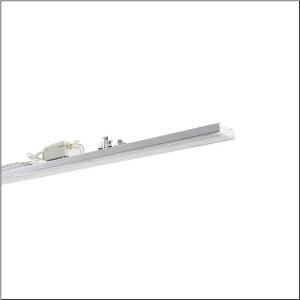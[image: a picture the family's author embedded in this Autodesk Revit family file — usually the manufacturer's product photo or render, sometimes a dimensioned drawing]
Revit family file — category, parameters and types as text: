
# Revit family: licross_11_recessed_mo_51tl14dn325g
name_source: partatom
category: Lighting Fixtures
units: mm (PartAtom-declared; Revit-internal decimal feet)

## family parameters
Cut with Voids When Loaded = No
Host = Face
Light Source = No
Part Type = Normal
Room Calculation Point = No
Round Connector Dimension = Use Diameter
Shared = No

## types (1)
- --- (1 x LED, 2900 lm, 17.6 W, 3000K)
    Apparent Load = 18 VA
    CIE Flux Codes = 56 84 97 100 100
    Color Rendering = 80
    Color Temperature = 3000K
    Default Elevation = 1800 mm
    Description = Licross 11 Recessed MO, luminaire insert, of sheet steel, coil coated, white, length: 1.500mm, width: 66mm, height: 67mm, LED rated luminous flux: 2.900lm, light colour: 830, SDCM (Standard Deviation of Colour Matching)MacAdam ≤ 2 SDCM (initial), control gear: DALI 2, with plug, 5-pole, with phase selection, mains connection: 220..240V, AC, 50/60Hz, rated input power: 17.6W, internal wiring halogen-free, primary light control with lens, of plastic, primary optical cover: cover, of PMMA, light emission: direct distribution, primary light characteristic: asymmetric, protection rating (complete): IP40, insulation class (complete): insulation class I (protective earthing), certification: CE, ENEC, VDE, UKCA, protection symbol: D if used in an environment without relevant dust loads with corresponding accessories, impact resistance: IK06, permissible ambient temperature for indoor applications: -25..+50°C, corresponds to IFS (International Featured Standards) requirements for safety and quality in the food industry, reducing of maximum allowable ambient temperature of 5°C with ceiling mounting, LABS conformity tested according to VDMA 24364:2018-05, The light source and the operating device comply with the requirements of the Ecodesign Regulation (EU) 2019/2020 and are replaceable in accordance with this regulation, packaging unit: 1 piece
    Height = 58 mm
    Lamp = 1 x LED
    Lamp Light Flux = 2900 lm
    Lamp Power = 17.6 W
    Lamp count = 1
    Length = 1500 mm
    Luminous efficacy = 165 lm/W
    Manufacturer = Siteco
    ModVariant = No
    Model = 51TL14DN325G
    Mounting Place = Ceiling
    Mounting Type = Pendant
    Number of Poles = 1
    OnlyDefault = Yes
    Power Factor = 1
    Product Name = Licross 11 Recessed MO
    Product group = luminaire insert | ceiling pendant
    ProductGroupID = 901
    Protection Class = Protection class I
    Protection Degree = IP 40
    RLX_Detail_Level = 1
    RLX_Emergency_Light_Flux = 0 lm
    RLX_Emergency_Type = 0
    RLX_Emergency_Type_DB = No
    RlxData = <blob elided: 24953 chars, md5=e817cd5a>
    Socket = socket
    Standby Power = 0 W
    System Light Flux = 2900 lm
    System Power = 18 W
    Type Comments = factory setting: luminous flux: 100 % | dim-lin: 254 | 114 mA
    Type Image = l_1296930.jpg
    URL = http://relux.com
    VarID = @adj_077063
    Voltage = 0 V
    Weight = 0.00 kg
    Width = 66 mm

## geometry (parser evidence)
native form markers: Blend x4, Sweep x10
no freeform markers — native parametric forms only
